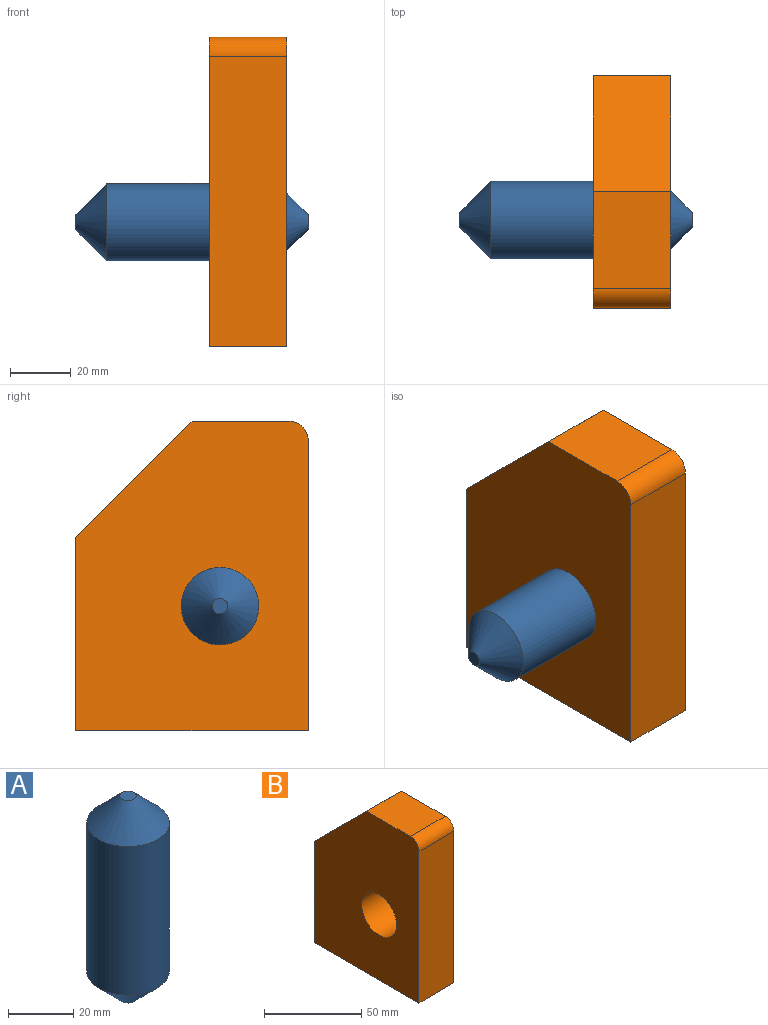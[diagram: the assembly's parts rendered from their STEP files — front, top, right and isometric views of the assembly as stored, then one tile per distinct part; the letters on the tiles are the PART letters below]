
ASSEMBLY  parts=2 mates=1
PART A: 5 faces, bbox 25.4x25.4x76.2 mm
  f0: cylinder r=12.7mm len=55.88mm, axis (0,0,-1), area 4459mm2, adj f3,f4
  f1: plane 5.08x5.08mm, normal (0,0,1), area 20.3mm2, adj f3
  f2: plane 5.08x5.08mm, normal (0,0,-1), area 20.3mm2, adj f4
  f3: cone r=2.54mm half-angle=45deg, axis (0,0,-1), area 687.9mm2, adj f0,f1
  f4: cone r=12.7mm half-angle=45deg, axis (0,0,1), area 687.9mm2, adj f0,f2
PART B: 9 faces, bbox 25.4x76.2x101.6 mm
  f0: plane 31.75x25.4mm, normal (0,0,1), area 806.5mm2, adj f5,f6,f7,f8
  f1: plane 95.25x25.4mm, normal (0,-1,0), area 2419.3mm2, adj f2,f5,f6,f7
  f2: plane 76.2x25.4mm, normal (0,0,-1), area 1935.5mm2, adj f1,f4,f5,f6
  f3: cylinder r=12.7mm len=25.4mm, axis (-1,0,0), area 2026.8mm2, adj f5,f6
  f4: plane 63.5x25.4mm, normal (0,1,0), area 1612.9mm2, adj f2,f5,f6,f8
  f5: plane 101.6x76.2mm, normal (1,0,0), area 6500.8mm2, adj f0,f1,f2,f3,f4,f7,f8
  f6: plane 101.6x76.2mm, normal (-1,0,0), area 6500.8mm2, adj f0,f1,f2,f3,f4,f7,f8
  f7: cylinder r=6.35mm len=25.4mm, axis (1,0,0), area 253.4mm2, adj f0,f1,f5,f6
  f8: plane 38.1x38.1mm, normal (0,0.71,0.71), area 1368.6mm2, adj f0,f4,f5,f6
PLACE A rot(axis=(0.58,0.58,0.58),120deg) t=(-43.78,-49,-27.71)mm
PLACE B at identity fixed
MATE slider B.f3 <-> A.f0  axis (-1,0,0) through (25.4,-13.63,10.36)mm
